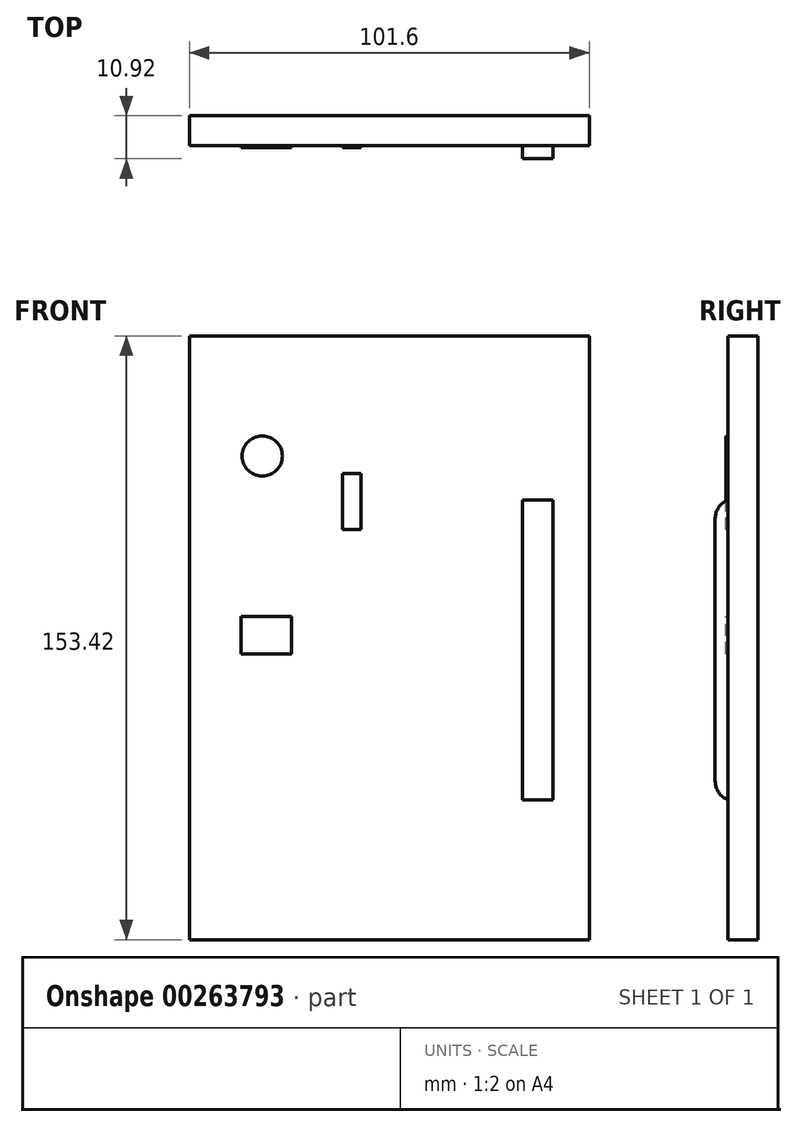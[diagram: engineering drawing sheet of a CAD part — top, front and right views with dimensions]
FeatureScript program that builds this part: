
annotation { "Feature Type Name" : "Feature", "Feature Type Description" : "" }
export const myFeature = defineFeature(function(context is Context, id is Id, definition is map)
    precondition{}
    {
        {
            var Q0;
            Q0=qCreatedBy(makeId("Top.planeOp"),FACE);
            var sketch = newSketch(context, id + "F0", { "sketchPlane" : qUnion([Q0])});
            skLineSegment(sketch, "E0.bottom", {"start": v(50.8, 3.81) * mm, "end": v(-50.8, 3.81) * mm});
            skLineSegment(sketch, "E0.top", {"start": v(50.8, -3.81) * mm, "end": v(-50.8, -3.81) * mm});
            skLineSegment(sketch, "E0.left", {"start": v(50.8, 3.81) * mm, "end": v(50.8, -3.81) * mm});
            skLineSegment(sketch, "E0.right", {"start": v(-50.8, 3.81) * mm, "end": v(-50.8, -3.81) * mm});
            skPoint(sketch, "E0.middle", {"position": v(0, 0) * mm});
            skSolve(sketch);
        }
        {
            var Q0;
            Q0 = qSketchRegion(id + "F0", true);
            extrude(context, id + "F1", {"entities" : qUnion([Q0]), "depth" : 153.42 * mm});
        }
        {
            var Q0;
            Q0=makeQuery(id+"F1.opExtrude","SWEPT_FACE",FACE,{"disambiguationData":[OSD([sQuery(id+"F0.wireOp",EDGE,"E0.top")])]});
            var sketch = newSketch(context, id + "F2", { "sketchPlane" : qUnion([Q0])});
            skLineSegment(sketch, "E1.bottom", {"start": v(33.91, 111.74) * mm, "end": v(41.53, 111.74) * mm});
            skLineSegment(sketch, "E1.top", {"start": v(33.91, 35.54) * mm, "end": v(41.53, 35.54) * mm});
            skLineSegment(sketch, "E1.left", {"start": v(33.91, 111.74) * mm, "end": v(33.91, 35.54) * mm});
            skLineSegment(sketch, "E1.right", {"start": v(41.53, 111.74) * mm, "end": v(41.53, 35.54) * mm});
            skSolve(sketch);
        }
        {
            var Q0;
            Q0 = qSketchRegion(id + "F2", true);
            extrude(context, id + "F3", {"entities" : qUnion([Q0]), "operationType" : NewBodyOperationType.ADD, "depth" : 3.3 * mm});
        }
        {
            var Q0;
            Q0=makeQuery(id+"F3.opExtrude","CAP_EDGE",EDGE,{"disambiguationData":[OSD([sQuery(id+"F2.wireOp",EDGE,"E1.bottom")])],"isStart":false});
            var Q1;
            Q1=makeQuery(id+"F3.opExtrude","CAP_EDGE",EDGE,{"disambiguationData":[OSD([sQuery(id+"F2.wireOp",EDGE,"E1.top")])],"isStart":false});
            fillet(context, id + "F4", {"entities" : qUnion([Q0, Q1]), "radius" : 5.08 * mm, "tangentPropagation" : true, "allowEdgeOverflow" : false});
        }
        {
            var Q0;
            Q0=makeQuery(id+"F1.opExtrude","SWEPT_FACE",FACE,{"disambiguationData":[OSD([sQuery(id+"F0.wireOp",EDGE,"E0.top")])]});
            var sketch = newSketch(context, id + "F5", { "sketchPlane" : qUnion([Q0])});
            skCircle(sketch, "E2", {"center": v(-32.26, 122.9) * mm, "radius": 5.1 * mm});
            skLineSegment(sketch, "E3.bottom", {"start": v(-7.13, 104.22) * mm, "end": v(-11.89, 104.22) * mm});
            skLineSegment(sketch, "E3.top", {"start": v(-7.13, 118.48) * mm, "end": v(-11.89, 118.48) * mm});
            skLineSegment(sketch, "E3.left", {"start": v(-7.13, 104.22) * mm, "end": v(-7.13, 118.48) * mm});
            skLineSegment(sketch, "E3.right", {"start": v(-11.89, 104.22) * mm, "end": v(-11.89, 118.48) * mm});
            skPoint(sketch, "E3.middle", {"position": v(-9.5, 111.35) * mm});
            skLineSegment(sketch, "E4.bottom", {"start": v(-24.8, 72.63) * mm, "end": v(-37.7, 72.63) * mm});
            skLineSegment(sketch, "E4.top", {"start": v(-24.8, 82.14) * mm, "end": v(-37.7, 82.14) * mm});
            skLineSegment(sketch, "E4.left", {"start": v(-24.8, 72.63) * mm, "end": v(-24.8, 82.14) * mm});
            skLineSegment(sketch, "E4.right", {"start": v(-37.7, 72.63) * mm, "end": v(-37.7, 82.14) * mm});
            skPoint(sketch, "E4.middle", {"position": v(-31.24, 77.39) * mm});
            skSolve(sketch);
        }
        {
            var Q0;
            Q0 = qSketchRegion(id + "F5", true);
            extrude(context, id + "F6", {"entities" : qUnion([Q0]), "operationType" : NewBodyOperationType.ADD, "depth" : 0.5 * mm});
        }
    });
